FCSTD DOCUMENT  (FreeCAD 0.19R)
Label: base
License: Creative Commons Attribution-ShareAlike
LicenseURL: http://creativecommons.org/licenses/by-sa/4.0/
objects: Sketcher::SketchObject×6, PartDesign::Plane×5, Spreadsheet::Sheet×1, PartDesign::Body×1, App::Part×1
note: 12 computed .brp shape members not serialized (recipe doc carries the construction recipe); baked Part::Feature solids carry a one-line shape summary decoded from their .brp

FEATURE [PartDesign::Plane] DatumPlane  label="bottom_in_DatumPlane"
  AttachmentOffset = pos=(0,0,-25) rot=(0,0,1;0rad)
  Length = 60
  MapMode = 5
  Placement = pos=(0,0,-25) rot=(0,0,1;0rad)
  ResizeMode = 0
  Support = -> [XY_Plane001]
  Width = 60
  expr: .AttachmentOffset.Base.z = <<base_values>>.height / -2
FEATURE [Spreadsheet::Sheet] Spreadsheet  label="base_values"
  cells = A2=wood; B2(wood)==3mm; A4=height; B4(height)==50mm; A5=width; B5(width)==100mm; A6=depth; B6(depth)==80mm; A8=height_in; B8(height_in)==height; A9=width_in; B9(width_in)==width - 2 * wood; A10=depth_in; B10(depth_in)==depth - 2 * wood
FEATURE [PartDesign::Plane] DatumPlane001  label="front_in_DatumPlane001"
  AttachmentOffset = pos=(0,0,40) rot=(0,0,1;0rad)
  Length = 60
  MapMode = 5
  Placement = pos=(0,-40,-8.9e-15) rot=(1,0,0;1.5708rad)
  ResizeMode = 0
  Support = -> [XZ_Plane001]
  Width = 60
  expr: .AttachmentOffset.Base.z = <<base_values>>.depth / 2
FEATURE [PartDesign::Plane] DatumPlane002  label="right_in_DatumPlane002"
  AttachmentOffset = pos=(0,0,47) rot=(0,0,1;0rad)
  Length = 60
  MapMode = 5
  Placement = pos=(47,-1.04e-14,1.04e-14) rot=(0.57735,0.57735,0.57735;2.0944rad)
  ResizeMode = 0
  Support = -> [YZ_Plane001]
  Width = 60
  expr: .AttachmentOffset.Base.z = <<base_values>>.width_in / 2
FEATURE [Sketcher::SketchObject] Sketch  label="bottom_outline"
  FullyConstrained = true
  MapMode = 5
  Placement = pos=(0,0,-25) rot=(0,0,1;0rad)
  Support = -> [DatumPlane]
  expr: .Constraints.depth = <<base_values>>.depth
  expr: .Constraints.width = <<base_values>>.width
  sketch-geometry (4):
    g0: LineSegment StartX=-50 StartY=40 StartZ=0 EndX=50 EndY=40 EndZ=0
    g1: LineSegment StartX=50 StartY=40 StartZ=0 EndX=50 EndY=-40 EndZ=0
    g2: LineSegment StartX=50 StartY=-40 StartZ=0 EndX=-50 EndY=-40 EndZ=0
    g3: LineSegment StartX=-50 StartY=-40 StartZ=0 EndX=-50 EndY=40 EndZ=0
  constraints (11):
    c: Coincident(g0,g1)
    c: Coincident(g1,g2)
    c: Coincident(g2,g3)
    c: Coincident(g3,g0)
    c: Horizontal(g0)
    c: Horizontal(g2)
    c: Vertical(g1)
    c: Vertical(g3)
    c: Symmetric(g2,g0,g-1)
    c: DistanceY(g3,g3) = 80  'depth'
    c: DistanceX(g0,g0) = 100  'width'
FEATURE [Sketcher::SketchObject] Sketch001  label="front_outline"
  FullyConstrained = true
  MapMode = 5
  Placement = pos=(0,-40,-8.9e-15) rot=(1,0,0;1.5708rad)
  Support = -> [DatumPlane001]
  expr: .Constraints.width = <<base_values>>.width
  expr: .Constraints.height = <<base_values>>.height
  sketch-geometry (4):
    g0: LineSegment StartX=-50 StartY=25 StartZ=0 EndX=50 EndY=25 EndZ=0
    g1: LineSegment StartX=50 StartY=25 StartZ=0 EndX=50 EndY=-25 EndZ=0
    g2: LineSegment StartX=50 StartY=-25 StartZ=0 EndX=-50 EndY=-25 EndZ=0
    g3: LineSegment StartX=-50 StartY=-25 StartZ=0 EndX=-50 EndY=25 EndZ=0
  constraints (11):
    c: Coincident(g0,g1)
    c: Coincident(g1,g2)
    c: Coincident(g2,g3)
    c: Coincident(g3,g0)
    c: Horizontal(g0)
    c: Horizontal(g2)
    c: Vertical(g1)
    c: Vertical(g3)
    c: Symmetric(g2,g0,g-1)
    c: DistanceX(g0,g0) = 100  'width'
    c: DistanceY(g3,g3) = 50  'height'
FEATURE [Sketcher::SketchObject] Sketch002  label="right_outline"
  FullyConstrained = true
  MapMode = 5
  Placement = pos=(47,-1.04e-14,1.04e-14) rot=(0.57735,0.57735,0.57735;2.0944rad)
  Support = -> [DatumPlane002]
  expr: .Constraints.height = <<base_values>>.height
  expr: .Constraints.depth = <<base_values>>.depth
  sketch-geometry (4):
    g0: LineSegment StartX=-40 StartY=25 StartZ=0 EndX=40 EndY=25 EndZ=0
    g1: LineSegment StartX=40 StartY=25 StartZ=0 EndX=40 EndY=-25 EndZ=0
    g2: LineSegment StartX=40 StartY=-25 StartZ=0 EndX=-40 EndY=-25 EndZ=0
    g3: LineSegment StartX=-40 StartY=-25 StartZ=0 EndX=-40 EndY=25 EndZ=0
  constraints (11):
    c: Coincident(g0,g1)
    c: Coincident(g1,g2)
    c: Coincident(g2,g3)
    c: Coincident(g3,g0)
    c: Horizontal(g0)
    c: Horizontal(g2)
    c: Vertical(g1)
    c: Vertical(g3)
    c: DistanceY(g3,g3) = 50  'height'
    c: DistanceX(g0,g0) = 80  'depth'
    c: Symmetric(g2,g0,g-1)
FEATURE [PartDesign::Plane] DatumPlane003  label="top_in_DatumPlane003"
  AttachmentOffset = pos=(0,0,50) rot=(0,0,1;0rad)
  Length = 60
  MapMode = 5
  Placement = pos=(0,0,25) rot=(0,0,1;0rad)
  ResizeMode = 0
  Support = -> [DatumPlane]
  Width = 60
  expr: .AttachmentOffset.Base.z = <<base>>#<<base_values>>.height
FEATURE [Sketcher::SketchObject] Sketch003  label="top_outline"
  FullyConstrained = true
  MapMode = 5
  Placement = pos=(0,0,25) rot=(0,0,1;0rad)
  Support = -> [DatumPlane003]
  expr: .Constraints.width = <<base_values>>.width
  expr: .Constraints.depth = <<base_values>>.depth
  sketch-geometry (4):
    g0: LineSegment StartX=-50 StartY=40 StartZ=0 EndX=50 EndY=40 EndZ=0
    g1: LineSegment StartX=50 StartY=40 StartZ=0 EndX=50 EndY=-40 EndZ=0
    g2: LineSegment StartX=50 StartY=-40 StartZ=0 EndX=-50 EndY=-40 EndZ=0
    g3: LineSegment StartX=-50 StartY=-40 StartZ=0 EndX=-50 EndY=40 EndZ=0
  constraints (11):
    c: Coincident(g0,g1)
    c: Coincident(g1,g2)
    c: Coincident(g2,g3)
    c: Coincident(g3,g0)
    c: Horizontal(g0)
    c: Horizontal(g2)
    c: Vertical(g1)
    c: Vertical(g3)
    c: Symmetric(g2,g0,g-1)
    c: DistanceY(g3,g3) = 80  'depth'
    c: DistanceX(g0,g0) = 100  'width'
FEATURE [Sketcher::SketchObject] Sketch004  label="joint_right_base"
  FullyConstrained = true
  MapMode = 5
  Placement = pos=(0,0,25) rot=(0,0,1;0rad)
  Support = -> [DatumPlane003]
  expr: .Constraints.width_in = <<base_values>>.width_in
  expr: .Constraints.finger_width = <<base_values>>.wood * 4
  expr: .Constraints.depth_in = <<base_values>>.depth_in
  expr: Constraints[21] = <<base_values>>.wood * 3
  expr: Constraints[23] = <<base_values>>.wood
  sketch-geometry (8):
    g0: LineSegment StartX=-47 StartY=0 StartZ=0 EndX=47 EndY=0 EndZ=0
    g1: LineSegment StartX=47 StartY=-22 StartZ=0 EndX=47 EndY=22 EndZ=0
    g2: LineSegment StartX=47 StartY=-16 StartZ=0 EndX=50 EndY=-16 EndZ=0
    g3: LineSegment StartX=50 StartY=-16 StartZ=0 EndX=50 EndY=-28 EndZ=0
    g4: LineSegment StartX=50 StartY=-28 StartZ=0 EndX=47 EndY=-28 EndZ=0
    g5: LineSegment StartX=47 StartY=-28 StartZ=0 EndX=47 EndY=-16 EndZ=0
    g6: LineSegment StartX=47 StartY=-22 StartZ=0 EndX=47 EndY=-37 EndZ=0
    g7: LineSegment StartX=47 StartY=37 StartZ=0 EndX=47 EndY=22 EndZ=0
  constraints (25):
    c: Horizontal(g0)
    c: Symmetric(g0,g0,g-1)
    c: DistanceX(g0,g0) = 94  'width_in'
    c: Vertical(g1)
    c: Symmetric(g1,g1,g0)
    c: Coincident(g2,g3)
    c: Coincident(g3,g4)
    c: Coincident(g4,g5)
    c: Coincident(g5,g2)
    c: Horizontal(g2)
    c: Horizontal(g4)
    c: Vertical(g3)
    c: Vertical(g5)
    c: Symmetric(g5,g5,g1)
    c: DistanceY(g3,g3) = 12  'finger_width'
    c: Vertical(g6)
    c: Vertical(g7)
    c: Coincident(g7,g1)
    c: Equal(g7,g6)
    c: Coincident(g6,g1)
    c: DistanceY(g6,g7) = 74  'depth_in'
    c: DistanceY(g6,g4) = 9
    c: DistanceY(g1,g1) = 44  'array_y'
    c: DistanceX(g2,g2) = 3
    c: DistanceY(g1) = -22  'pos_y'
FEATURE [PartDesign::Plane] DatumPlane004  label="joint_right_top_DatumPlane004"
  AttachmentOffset = pos=(47,-22,0) rot=(0,0,1;0rad)
  Length = 84
  MapMode = 5
  Placement = pos=(47,-22,25) rot=(0,0,1;0rad)
  ResizeMode = 0
  Support = -> [DatumPlane003]
  Width = 62
  expr: .AttachmentOffset.Base.y = <<joint_right_base>>.Constraints.pos_y
  expr: .AttachmentOffset.Base.x = <<base_values>>.width_in / 2
FEATURE [Sketcher::SketchObject] Sketch005  label="joint_right_top"
  FullyConstrained = true
  MapMode = 5
  Placement = pos=(47,-22,25) rot=(0,0,1;0rad)
  Support = -> [DatumPlane004]
  expr: .Constraints.finger_width = <<joint_right_base>>.Constraints.finger_width
  expr: .Constraints.width = <<base_values>>.wood
  sketch-geometry (4):
    g0: LineSegment StartX=0 StartY=6 StartZ=0 EndX=3 EndY=6 EndZ=0
    g1: LineSegment StartX=3 StartY=6 StartZ=0 EndX=3 EndY=-6 EndZ=0
    g2: LineSegment StartX=3 StartY=-6 StartZ=0 EndX=0 EndY=-6 EndZ=0
    g3: LineSegment StartX=0 StartY=-6 StartZ=0 EndX=0 EndY=6 EndZ=0
  constraints (11):
    c: Coincident(g0,g1)
    c: Coincident(g1,g2)
    c: Coincident(g2,g3)
    c: Coincident(g3,g0)
    c: Horizontal(g0)
    c: Horizontal(g2)
    c: Vertical(g1)
    c: Vertical(g3)
    c: Symmetric(g3,g3,g-1)
    c: DistanceX(g0,g0) = 3  'width'
    c: DistanceY(g1,g1) = 12  'finger_width'
FEATURE [PartDesign::Body] Body  label="box"
  Group = -> [DatumPlane,DatumPlane001,DatumPlane002,Sketch,Sketch001,Sketch002,DatumPlane003,Sketch003,Sketch004,DatumPlane004,Sketch005]
  Origin = -> Origin001
FEATURE [App::Part] Part  label="base_dimensions_Part"
  Group = -> [Body]
  Origin = -> Origin
